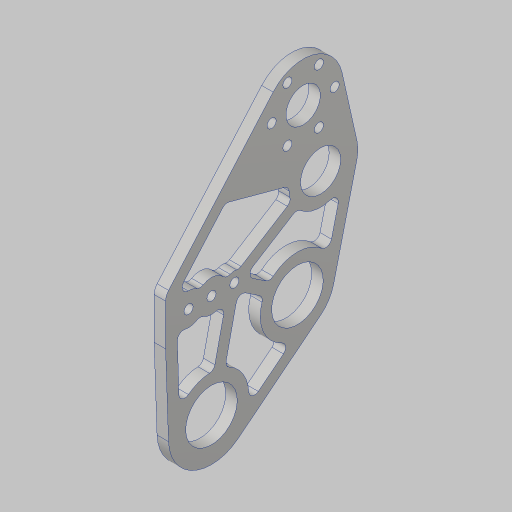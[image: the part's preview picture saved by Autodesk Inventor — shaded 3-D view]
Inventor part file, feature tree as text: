
AUTODESK INVENTOR PART (.ipt)
format: ipt  version: 2023.5 (Build 275446000, 446)  size: 297,472 bytes
history: native  units: in
note: dims shown in document units (in); Inventor stores cm internally (conversion verified against a paired STEP export)
features: sketch x2, extrude x2, fillet x2, hole x1, projected_geometry x1
ambient origin geometry x8: Origin, YZ Plane, XZ Plane, XY Plane, X Axis, Y Axis, Z Axis, Center Point
bodies: Solid1 (feature_tree)
feature tree (8):
  sketch  "Sketch1"  dims[d0=1.0in d1=2.0in]
  extrude  "Extrusion1"  Depth=2.0in
  hole  "Hole1"  [1 undecoded]
  extrude  "Extrusion2"  Depth=0.26in
  fillet  "Fillet1"  Radius=5.0in
  fillet  "Fillet2"  Radius=1.949in
  sketch  "Sketch2"  dims[d2=1.125in d3=2.25in d4=3.0in d5=5.0in d6=1.949in d11=0.5in d12=0.5in d13=0.375in d18=0.4688in d19=2.5in d20=1.375in d21=1.74in d22=8.0in d23=1.0in d24=2.1066in d25=0.25in d26=0.0in d27=0.75in d29=2.3622in d31=360.0deg d33=0.201in d34=0.75in d35=0.385in d36=0.25in d37=0.5635in d38=1.0in d39=0.8108in d40=1.0in d41=3.3in d42=1.6in d43=3.0in d44=1.4348in d46=0.25in d48=0.5in d49=1.0in d50=0.875in d51=0.875in d52=0.25in d53=0.25in d54=0.25in d55=0.125in d56=0.25in d57=0.125in d58=0.125in d59=0.125in d60=0.125in d61=0.125in d62=0.25in d63=1.0in d64=0.0in d65=0.13in d66=0.26in]
  projected_geometry  "Project Cut Edges1"
note: 1 required parameter value undecoded (feature->parameter linkage not recoverable at this tier; creation-order binding heuristic only, values carry confidence <= 0.55)
